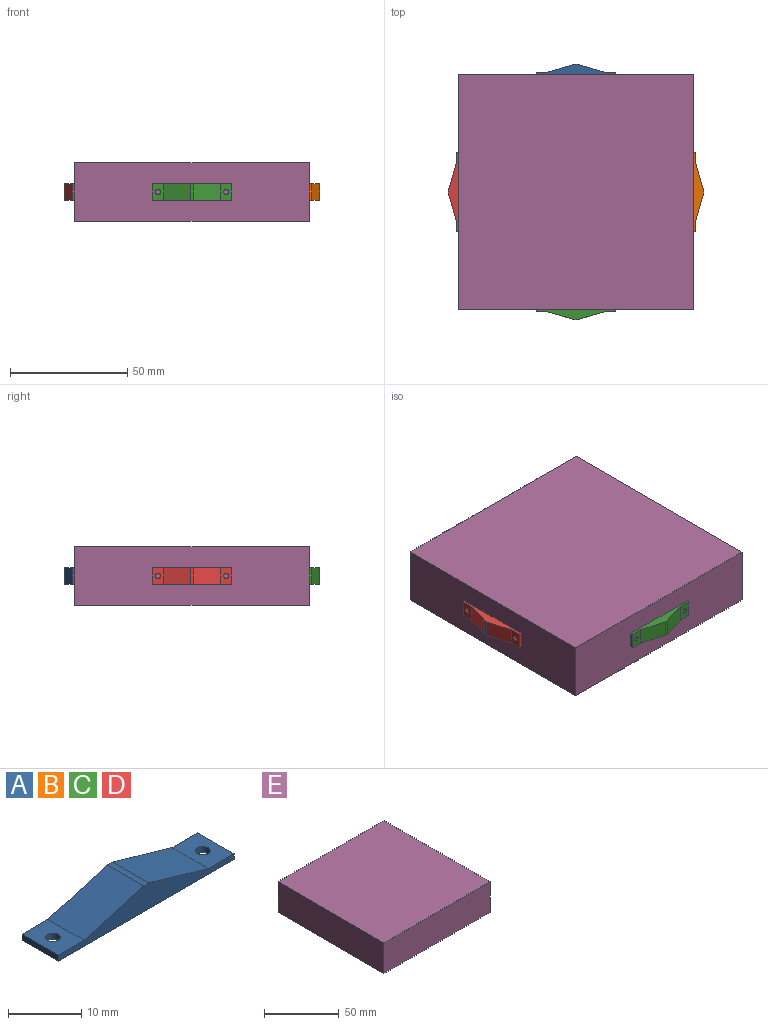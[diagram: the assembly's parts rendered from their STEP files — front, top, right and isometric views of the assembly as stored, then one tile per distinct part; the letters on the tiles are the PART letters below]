
ASSEMBLY  parts=5 mates=4
PART A: 12 faces, bbox 34x7x4.4 mm
  f0: plane 7x1mm, normal (-1,0,0), area 7mm2, adj f1,f6,f7,f8
  f1: plane 34x7mm, normal (0,0,-1), area 231.7mm2, adj f0,f2,f7,f8,f10,f11
  f2: plane 7x1mm, normal (1,0,0), area 7mm2, adj f1,f3,f7,f8
  f3: plane 7x5mm, normal (0,0,1), area 31.9mm2, adj f2,f4,f7,f8,f11
  f4: plane 11.52x7mm, normal (0.28,0,0.96), area 84mm2, adj f3,f7,f8,f9
  f5: plane 11.52x7mm, normal (-0.28,0,0.96), area 84mm2, adj f6,f7,f8,f9
  f6: plane 7x5mm, normal (0,0,1), area 31.9mm2, adj f0,f5,f7,f8,f10
  f7: plane 34x4.36mm, normal (0,-1,0), area 75.9mm2, adj f0,f1,f2,f3,f4,f5,f6,f9
  f8: plane 34x4.36mm, normal (0,1,0), area 75.9mm2, adj f0,f1,f2,f3,f4,f5,f6,f9
  f9: plane 7x0.96mm, normal (0,0,1), area 6.7mm2, adj f4,f5,f7,f8
  f10: cylinder r=1mm len=2mm, axis (0,0,1), area 6.3mm2, adj f1,f6
  f11: cylinder r=1mm len=2mm, axis (0,0,1), area 6.3mm2, adj f1,f3
PART B: same geometry as A
PART C: same geometry as A
PART D: same geometry as A
PART E: 6 faces, bbox 100x100x25 mm
  f0: plane 100x25mm, normal (-1,0,0), area 2500mm2, adj f1,f3,f4,f5
  f1: plane 100x25mm, normal (0,-1,0), area 2500mm2, adj f0,f2,f4,f5
  f2: plane 100x25mm, normal (1,0,0), area 2500mm2, adj f1,f3,f4,f5
  f3: plane 100x25mm, normal (0,1,0), area 2500mm2, adj f0,f2,f4,f5
  f4: plane 100x100mm, normal (0,0,1), area 10000mm2, adj f0,f1,f2,f3
  f5: plane 100x100mm, normal (0,0,-1), area 10000mm2, adj f0,f1,f2,f3
PLACE A rot(axis=(-1,0,0),90deg) t=(-2.49,42.31,9)mm
PLACE B rot(axis=(-0.58,0.58,-0.58),120deg) t=(47.51,-7.69,9)mm
PLACE C rot(axis=(1,0,0),90deg) t=(-2.49,-57.69,16)mm
PLACE D rot(axis=(0.58,-0.58,-0.58),120deg) t=(-52.49,-7.69,16)mm
PLACE E at identity
MATE parallel B.f1 <-> E.f2  axis (-1,0,0) through (47.51,-7.69,12.5)mm
MATE parallel D.f1 <-> E.f0  axis (1,0,0) through (-52.49,-7.69,12.5)mm
MATE parallel A.f1 <-> E.f3  axis (0,-1,0) through (-2.49,42.31,12.5)mm
MATE parallel C.f1 <-> E.f1  axis (0,1,0) through (-2.49,-57.69,12.5)mm
